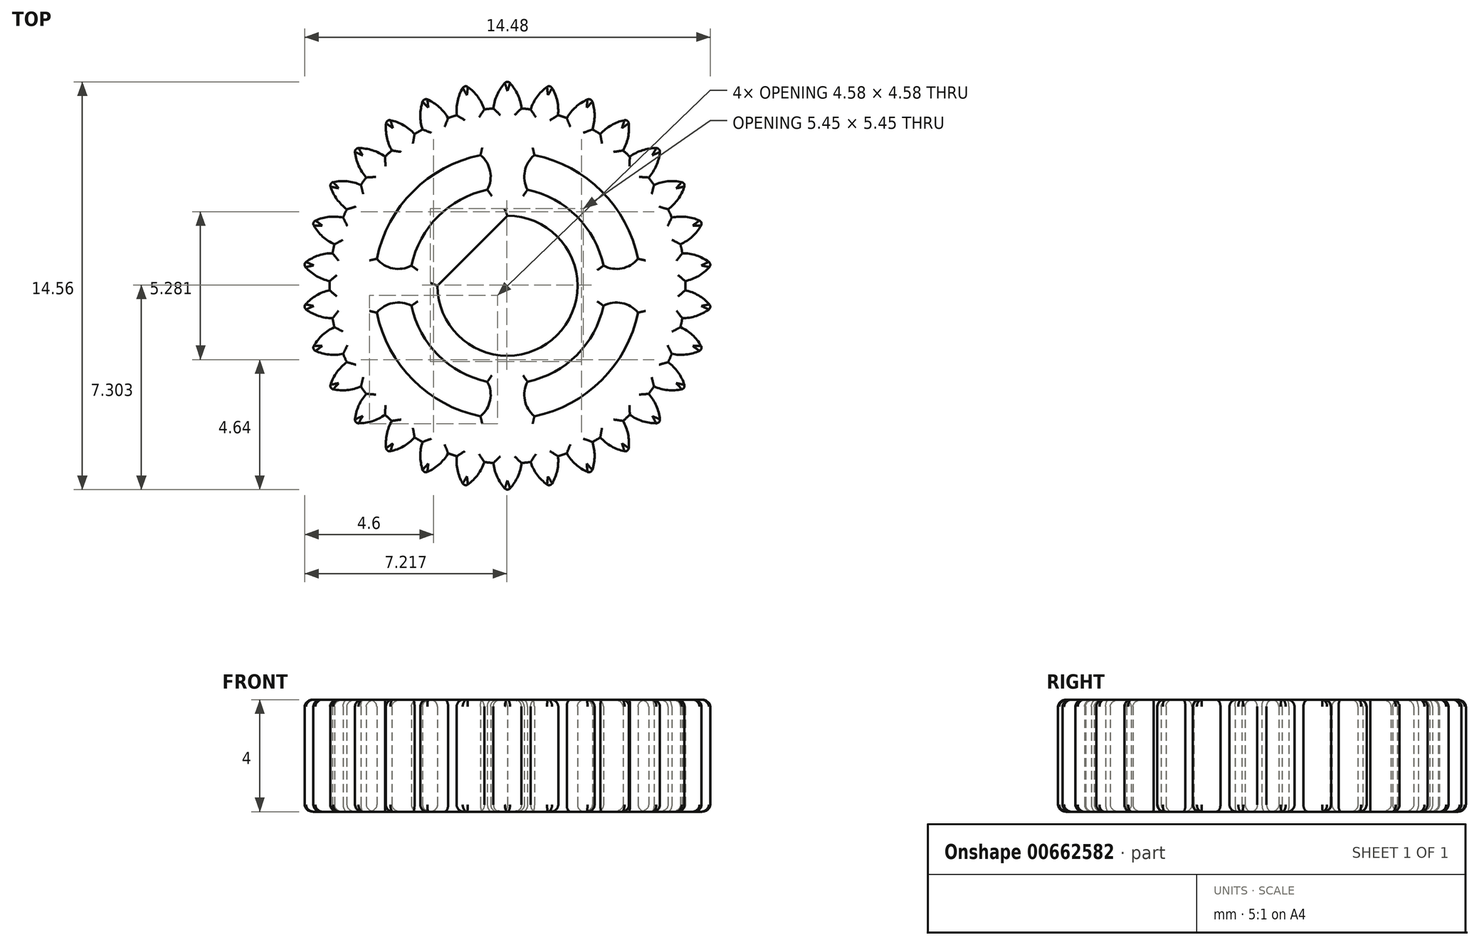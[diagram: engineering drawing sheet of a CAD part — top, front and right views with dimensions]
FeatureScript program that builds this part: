
annotation { "Feature Type Name" : "Feature", "Feature Type Description" : "" }
export const myFeature = defineFeature(function(context is Context, id is Id, definition is map)
    precondition{}
    {
        {
            var Q0;
            Q0=qCreatedBy(makeId("Top.planeOp"),FACE);
            var sketch = newSketch(context, id + "F0", { "sketchPlane" : qUnion([Q0])});
            skCircle(sketch, "E0", {"center": v(0, 0) * mm, "radius": 6.35 * mm});
            skCircle(sketch, "E1", {"center": v(0, 0) * mm, "radius": 4.76 * mm});
            skCircle(sketch, "E2", {"center": v(0, 0) * mm, "radius": 2.5 * mm});
            skCircle(sketch, "E3", {"center": v(0, 0) * mm, "radius": 3.5 * mm});
            skArc(sketch, "E4", {"start": v(-0.72, 3.43) * mm, "mid": v(-0.62, 4.09) * mm, "end": v(-0.96, 4.66) * mm});
            skLineSegment(sketch, "E5", {"start": v(0, 4.76) * mm, "end": v(0, 3.5) * mm});
            skArc(sketch, "E6.MirrorCS", {"start": v(0.72, 3.43) * mm, "mid": v(0.62, 4.09) * mm, "end": v(0.96, 4.66) * mm});
            skArc(sketch, "E7.1.0", {"start": v(-3.43, -0.72) * mm, "mid": v(-4.09, -0.62) * mm, "end": v(-4.66, -0.96) * mm});
            skArc(sketch, "E7.1.1", {"start": v(-3.43, 0.72) * mm, "mid": v(-4.09, 0.62) * mm, "end": v(-4.66, 0.96) * mm});
            skArc(sketch, "E7.2.0", {"start": v(0.72, -3.43) * mm, "mid": v(0.62, -4.09) * mm, "end": v(0.96, -4.66) * mm});
            skArc(sketch, "E7.2.1", {"start": v(-0.72, -3.43) * mm, "mid": v(-0.62, -4.09) * mm, "end": v(-0.96, -4.66) * mm});
            skArc(sketch, "E7.3.0", {"start": v(3.43, 0.72) * mm, "mid": v(4.09, 0.62) * mm, "end": v(4.66, 0.96) * mm});
            skArc(sketch, "E7.3.1", {"start": v(3.43, -0.72) * mm, "mid": v(4.09, -0.62) * mm, "end": v(4.66, -0.96) * mm});
            skLineSegment(sketch, "E8", {"start": v(0, 2.5) * mm, "end": v(-2.5, 0) * mm});
            skLineSegment(sketch, "E9", {"start": v(0, 7.33) * mm, "end": v(-0.5, 6.33) * mm});
            skLineSegment(sketch, "E10", {"start": v(0, 7.33) * mm, "end": v(0.5, 6.33) * mm});
            skArc(sketch, "E11", {"start": v(0, 7.33) * mm, "mid": v(-0.34, 6.88) * mm, "end": v(-0.5, 6.33) * mm});
            skLineSegment(sketch, "E12", {"start": v(0, 7.33) * mm, "end": v(0, 6.35) * mm});
            skArc(sketch, "E13.MirrorCS", {"start": v(0, 7.33) * mm, "mid": v(0.34, 6.88) * mm, "end": v(0.5, 6.33) * mm});
            skLineSegment(sketch, "E14.1.0", {"start": v(-1.52, 7.17) * mm, "end": v(-1.8, 6.09) * mm});
            skLineSegment(sketch, "E14.1.1", {"start": v(-1.52, 7.17) * mm, "end": v(-0.83, 6.3) * mm});
            skArc(sketch, "E14.1.2", {"start": v(-1.52, 7.17) * mm, "mid": v(-1.76, 6.65) * mm, "end": v(-1.8, 6.09) * mm});
            skArc(sketch, "E14.1.3", {"start": v(-1.52, 7.17) * mm, "mid": v(-1.1, 6.8) * mm, "end": v(-0.83, 6.3) * mm});
            skLineSegment(sketch, "E14.2.0", {"start": v(-2.98, 6.7) * mm, "end": v(-3.03, 5.58) * mm});
            skLineSegment(sketch, "E14.2.1", {"start": v(-2.98, 6.7) * mm, "end": v(-2.12, 5.99) * mm});
            skArc(sketch, "E14.2.2", {"start": v(-2.98, 6.7) * mm, "mid": v(-3.1, 6.14) * mm, "end": v(-3.03, 5.58) * mm});
            skArc(sketch, "E14.2.3", {"start": v(-2.98, 6.7) * mm, "mid": v(-2.49, 6.42) * mm, "end": v(-2.12, 5.99) * mm});
            skLineSegment(sketch, "E14.3.0", {"start": v(-4.3, 5.93) * mm, "end": v(-4.13, 4.83) * mm});
            skLineSegment(sketch, "E14.3.1", {"start": v(-4.3, 5.93) * mm, "end": v(-3.32, 5.42) * mm});
            skArc(sketch, "E14.3.2", {"start": v(-4.3, 5.93) * mm, "mid": v(-4.32, 5.36) * mm, "end": v(-4.13, 4.83) * mm});
            skArc(sketch, "E14.3.3", {"start": v(-4.3, 5.93) * mm, "mid": v(-3.77, 5.76) * mm, "end": v(-3.32, 5.42) * mm});
            skLineSegment(sketch, "E14.4.0", {"start": v(-5.45, 4.9) * mm, "end": v(-5.04, 3.86) * mm});
            skLineSegment(sketch, "E14.4.1", {"start": v(-5.45, 4.9) * mm, "end": v(-4.37, 4.6) * mm});
            skArc(sketch, "E14.4.2", {"start": v(-5.45, 4.9) * mm, "mid": v(-5.34, 4.35) * mm, "end": v(-5.04, 3.86) * mm});
            skArc(sketch, "E14.4.3", {"start": v(-5.45, 4.9) * mm, "mid": v(-4.88, 4.85) * mm, "end": v(-4.37, 4.6) * mm});
            skLineSegment(sketch, "E14.5.0", {"start": v(-6.35, 3.67) * mm, "end": v(-5.73, 2.73) * mm});
            skLineSegment(sketch, "E14.5.1", {"start": v(-6.35, 3.67) * mm, "end": v(-5.23, 3.6) * mm});
            skArc(sketch, "E14.5.2", {"start": v(-6.35, 3.67) * mm, "mid": v(-6.13, 3.14) * mm, "end": v(-5.73, 2.73) * mm});
            skArc(sketch, "E14.5.3", {"start": v(-6.35, 3.67) * mm, "mid": v(-5.78, 3.73) * mm, "end": v(-5.23, 3.6) * mm});
            skLineSegment(sketch, "E14.6.0", {"start": v(-6.97, 2.27) * mm, "end": v(-6.17, 1.48) * mm});
            skLineSegment(sketch, "E14.6.1", {"start": v(-6.97, 2.27) * mm, "end": v(-5.87, 2.43) * mm});
            skArc(sketch, "E14.6.2", {"start": v(-6.97, 2.27) * mm, "mid": v(-6.64, 1.8) * mm, "end": v(-6.17, 1.48) * mm});
            skArc(sketch, "E14.6.3", {"start": v(-6.97, 2.27) * mm, "mid": v(-6.43, 2.45) * mm, "end": v(-5.87, 2.43) * mm});
            skLineSegment(sketch, "E14.7.0", {"start": v(-7.3, 0.77) * mm, "end": v(-6.35, 0.16) * mm});
            skLineSegment(sketch, "E14.7.1", {"start": v(-7.3, 0.77) * mm, "end": v(-6.24, 1.16) * mm});
            skArc(sketch, "E14.7.2", {"start": v(-7.3, 0.77) * mm, "mid": v(-6.87, 0.38) * mm, "end": v(-6.35, 0.16) * mm});
            skArc(sketch, "E14.7.3", {"start": v(-7.3, 0.77) * mm, "mid": v(-6.8, 1.06) * mm, "end": v(-6.24, 1.16) * mm});
            skLineSegment(sketch, "E14.8.0", {"start": v(-7.3, -0.77) * mm, "end": v(-6.24, -1.16) * mm});
            skLineSegment(sketch, "E14.8.1", {"start": v(-7.3, -0.77) * mm, "end": v(-6.35, -0.16) * mm});
            skArc(sketch, "E14.8.2", {"start": v(-7.3, -0.77) * mm, "mid": v(-6.8, -1.06) * mm, "end": v(-6.24, -1.16) * mm});
            skArc(sketch, "E14.8.3", {"start": v(-7.3, -0.77) * mm, "mid": v(-6.87, -0.38) * mm, "end": v(-6.35, -0.16) * mm});
            skLineSegment(sketch, "E14.9.0", {"start": v(-6.97, -2.27) * mm, "end": v(-5.87, -2.43) * mm});
            skLineSegment(sketch, "E14.9.1", {"start": v(-6.97, -2.27) * mm, "end": v(-6.17, -1.48) * mm});
            skArc(sketch, "E14.9.2", {"start": v(-6.97, -2.27) * mm, "mid": v(-6.43, -2.45) * mm, "end": v(-5.87, -2.43) * mm});
            skArc(sketch, "E14.9.3", {"start": v(-6.97, -2.27) * mm, "mid": v(-6.64, -1.8) * mm, "end": v(-6.17, -1.48) * mm});
            skLineSegment(sketch, "E14.10.0", {"start": v(-6.35, -3.67) * mm, "end": v(-5.23, -3.6) * mm});
            skLineSegment(sketch, "E14.10.1", {"start": v(-6.35, -3.67) * mm, "end": v(-5.73, -2.73) * mm});
            skArc(sketch, "E14.10.2", {"start": v(-6.35, -3.67) * mm, "mid": v(-5.78, -3.73) * mm, "end": v(-5.23, -3.6) * mm});
            skArc(sketch, "E14.10.3", {"start": v(-6.35, -3.67) * mm, "mid": v(-6.13, -3.14) * mm, "end": v(-5.73, -2.73) * mm});
            skLineSegment(sketch, "E14.11.0", {"start": v(-5.45, -4.9) * mm, "end": v(-4.37, -4.6) * mm});
            skLineSegment(sketch, "E14.11.1", {"start": v(-5.45, -4.9) * mm, "end": v(-5.04, -3.86) * mm});
            skArc(sketch, "E14.11.2", {"start": v(-5.45, -4.9) * mm, "mid": v(-4.88, -4.85) * mm, "end": v(-4.37, -4.6) * mm});
            skArc(sketch, "E14.11.3", {"start": v(-5.45, -4.9) * mm, "mid": v(-5.34, -4.35) * mm, "end": v(-5.04, -3.86) * mm});
            skLineSegment(sketch, "E14.12.0", {"start": v(-4.3, -5.93) * mm, "end": v(-3.32, -5.42) * mm});
            skLineSegment(sketch, "E14.12.1", {"start": v(-4.3, -5.93) * mm, "end": v(-4.13, -4.83) * mm});
            skArc(sketch, "E14.12.2", {"start": v(-4.3, -5.93) * mm, "mid": v(-3.77, -5.76) * mm, "end": v(-3.32, -5.42) * mm});
            skArc(sketch, "E14.12.3", {"start": v(-4.3, -5.93) * mm, "mid": v(-4.32, -5.36) * mm, "end": v(-4.13, -4.83) * mm});
            skLineSegment(sketch, "E14.13.0", {"start": v(-2.98, -6.7) * mm, "end": v(-2.12, -5.99) * mm});
            skLineSegment(sketch, "E14.13.1", {"start": v(-2.98, -6.7) * mm, "end": v(-3.03, -5.58) * mm});
            skArc(sketch, "E14.13.2", {"start": v(-2.98, -6.7) * mm, "mid": v(-2.49, -6.42) * mm, "end": v(-2.12, -5.99) * mm});
            skArc(sketch, "E14.13.3", {"start": v(-2.98, -6.7) * mm, "mid": v(-3.1, -6.14) * mm, "end": v(-3.03, -5.58) * mm});
            skLineSegment(sketch, "E14.14.0", {"start": v(-1.52, -7.17) * mm, "end": v(-0.83, -6.3) * mm});
            skLineSegment(sketch, "E14.14.1", {"start": v(-1.52, -7.17) * mm, "end": v(-1.8, -6.09) * mm});
            skArc(sketch, "E14.14.2", {"start": v(-1.52, -7.17) * mm, "mid": v(-1.1, -6.8) * mm, "end": v(-0.83, -6.3) * mm});
            skArc(sketch, "E14.14.3", {"start": v(-1.52, -7.17) * mm, "mid": v(-1.76, -6.65) * mm, "end": v(-1.8, -6.09) * mm});
            skLineSegment(sketch, "E14.15.0", {"start": v(0, -7.33) * mm, "end": v(0.5, -6.33) * mm});
            skLineSegment(sketch, "E14.15.1", {"start": v(0, -7.33) * mm, "end": v(-0.5, -6.33) * mm});
            skArc(sketch, "E14.15.2", {"start": v(0, -7.33) * mm, "mid": v(0.34, -6.88) * mm, "end": v(0.5, -6.33) * mm});
            skArc(sketch, "E14.15.3", {"start": v(0, -7.33) * mm, "mid": v(-0.34, -6.88) * mm, "end": v(-0.5, -6.33) * mm});
            skLineSegment(sketch, "E14.16.0", {"start": v(1.52, -7.17) * mm, "end": v(1.8, -6.09) * mm});
            skLineSegment(sketch, "E14.16.1", {"start": v(1.52, -7.17) * mm, "end": v(0.83, -6.3) * mm});
            skArc(sketch, "E14.16.2", {"start": v(1.52, -7.17) * mm, "mid": v(1.76, -6.65) * mm, "end": v(1.8, -6.09) * mm});
            skArc(sketch, "E14.16.3", {"start": v(1.52, -7.17) * mm, "mid": v(1.1, -6.8) * mm, "end": v(0.83, -6.3) * mm});
            skLineSegment(sketch, "E14.17.0", {"start": v(2.98, -6.7) * mm, "end": v(3.03, -5.58) * mm});
            skLineSegment(sketch, "E14.17.1", {"start": v(2.98, -6.7) * mm, "end": v(2.12, -5.99) * mm});
            skArc(sketch, "E14.17.2", {"start": v(2.98, -6.7) * mm, "mid": v(3.1, -6.14) * mm, "end": v(3.03, -5.58) * mm});
            skArc(sketch, "E14.17.3", {"start": v(2.98, -6.7) * mm, "mid": v(2.49, -6.42) * mm, "end": v(2.12, -5.99) * mm});
            skLineSegment(sketch, "E14.18.0", {"start": v(4.3, -5.93) * mm, "end": v(4.13, -4.83) * mm});
            skLineSegment(sketch, "E14.18.1", {"start": v(4.3, -5.93) * mm, "end": v(3.32, -5.42) * mm});
            skArc(sketch, "E14.18.2", {"start": v(4.3, -5.93) * mm, "mid": v(4.32, -5.36) * mm, "end": v(4.13, -4.83) * mm});
            skArc(sketch, "E14.18.3", {"start": v(4.3, -5.93) * mm, "mid": v(3.77, -5.76) * mm, "end": v(3.32, -5.42) * mm});
            skLineSegment(sketch, "E14.19.0", {"start": v(5.45, -4.9) * mm, "end": v(5.04, -3.86) * mm});
            skLineSegment(sketch, "E14.19.1", {"start": v(5.45, -4.9) * mm, "end": v(4.37, -4.6) * mm});
            skArc(sketch, "E14.19.2", {"start": v(5.45, -4.9) * mm, "mid": v(5.34, -4.35) * mm, "end": v(5.04, -3.86) * mm});
            skArc(sketch, "E14.19.3", {"start": v(5.45, -4.9) * mm, "mid": v(4.88, -4.85) * mm, "end": v(4.37, -4.6) * mm});
            skLineSegment(sketch, "E14.20.0", {"start": v(6.35, -3.67) * mm, "end": v(5.73, -2.73) * mm});
            skLineSegment(sketch, "E14.20.1", {"start": v(6.35, -3.67) * mm, "end": v(5.23, -3.6) * mm});
            skArc(sketch, "E14.20.2", {"start": v(6.35, -3.67) * mm, "mid": v(6.13, -3.14) * mm, "end": v(5.73, -2.73) * mm});
            skArc(sketch, "E14.20.3", {"start": v(6.35, -3.67) * mm, "mid": v(5.78, -3.73) * mm, "end": v(5.23, -3.6) * mm});
            skLineSegment(sketch, "E14.21.0", {"start": v(6.97, -2.27) * mm, "end": v(6.17, -1.48) * mm});
            skLineSegment(sketch, "E14.21.1", {"start": v(6.97, -2.27) * mm, "end": v(5.87, -2.43) * mm});
            skArc(sketch, "E14.21.2", {"start": v(6.97, -2.27) * mm, "mid": v(6.64, -1.8) * mm, "end": v(6.17, -1.48) * mm});
            skArc(sketch, "E14.21.3", {"start": v(6.97, -2.27) * mm, "mid": v(6.43, -2.45) * mm, "end": v(5.87, -2.43) * mm});
            skLineSegment(sketch, "E14.22.0", {"start": v(7.3, -0.77) * mm, "end": v(6.35, -0.16) * mm});
            skLineSegment(sketch, "E14.22.1", {"start": v(7.3, -0.77) * mm, "end": v(6.24, -1.16) * mm});
            skArc(sketch, "E14.22.2", {"start": v(7.3, -0.77) * mm, "mid": v(6.87, -0.38) * mm, "end": v(6.35, -0.16) * mm});
            skArc(sketch, "E14.22.3", {"start": v(7.3, -0.77) * mm, "mid": v(6.8, -1.06) * mm, "end": v(6.24, -1.16) * mm});
            skLineSegment(sketch, "E14.23.0", {"start": v(7.3, 0.77) * mm, "end": v(6.24, 1.16) * mm});
            skLineSegment(sketch, "E14.23.1", {"start": v(7.3, 0.77) * mm, "end": v(6.35, 0.16) * mm});
            skArc(sketch, "E14.23.2", {"start": v(7.3, 0.77) * mm, "mid": v(6.8, 1.06) * mm, "end": v(6.24, 1.16) * mm});
            skArc(sketch, "E14.23.3", {"start": v(7.3, 0.77) * mm, "mid": v(6.87, 0.38) * mm, "end": v(6.35, 0.16) * mm});
            skLineSegment(sketch, "E14.24.0", {"start": v(6.97, 2.27) * mm, "end": v(5.87, 2.43) * mm});
            skLineSegment(sketch, "E14.24.1", {"start": v(6.97, 2.27) * mm, "end": v(6.17, 1.48) * mm});
            skArc(sketch, "E14.24.2", {"start": v(6.97, 2.27) * mm, "mid": v(6.43, 2.45) * mm, "end": v(5.87, 2.43) * mm});
            skArc(sketch, "E14.24.3", {"start": v(6.97, 2.27) * mm, "mid": v(6.64, 1.8) * mm, "end": v(6.17, 1.48) * mm});
            skLineSegment(sketch, "E14.25.0", {"start": v(6.35, 3.67) * mm, "end": v(5.23, 3.6) * mm});
            skLineSegment(sketch, "E14.25.1", {"start": v(6.35, 3.67) * mm, "end": v(5.73, 2.73) * mm});
            skArc(sketch, "E14.25.2", {"start": v(6.35, 3.67) * mm, "mid": v(5.78, 3.73) * mm, "end": v(5.23, 3.6) * mm});
            skArc(sketch, "E14.25.3", {"start": v(6.35, 3.67) * mm, "mid": v(6.13, 3.14) * mm, "end": v(5.73, 2.73) * mm});
            skLineSegment(sketch, "E14.26.0", {"start": v(5.45, 4.9) * mm, "end": v(4.37, 4.6) * mm});
            skLineSegment(sketch, "E14.26.1", {"start": v(5.45, 4.9) * mm, "end": v(5.04, 3.86) * mm});
            skArc(sketch, "E14.26.2", {"start": v(5.45, 4.9) * mm, "mid": v(4.88, 4.85) * mm, "end": v(4.37, 4.6) * mm});
            skArc(sketch, "E14.26.3", {"start": v(5.45, 4.9) * mm, "mid": v(5.34, 4.35) * mm, "end": v(5.04, 3.86) * mm});
            skLineSegment(sketch, "E14.27.0", {"start": v(4.3, 5.93) * mm, "end": v(3.32, 5.42) * mm});
            skLineSegment(sketch, "E14.27.1", {"start": v(4.3, 5.93) * mm, "end": v(4.13, 4.83) * mm});
            skArc(sketch, "E14.27.2", {"start": v(4.3, 5.93) * mm, "mid": v(3.77, 5.76) * mm, "end": v(3.32, 5.42) * mm});
            skArc(sketch, "E14.27.3", {"start": v(4.3, 5.93) * mm, "mid": v(4.32, 5.36) * mm, "end": v(4.13, 4.83) * mm});
            skLineSegment(sketch, "E14.28.0", {"start": v(2.98, 6.7) * mm, "end": v(2.12, 5.99) * mm});
            skLineSegment(sketch, "E14.28.1", {"start": v(2.98, 6.7) * mm, "end": v(3.03, 5.58) * mm});
            skArc(sketch, "E14.28.2", {"start": v(2.98, 6.7) * mm, "mid": v(2.49, 6.42) * mm, "end": v(2.12, 5.99) * mm});
            skArc(sketch, "E14.28.3", {"start": v(2.98, 6.7) * mm, "mid": v(3.1, 6.14) * mm, "end": v(3.03, 5.58) * mm});
            skLineSegment(sketch, "E14.29.0", {"start": v(1.52, 7.17) * mm, "end": v(0.83, 6.3) * mm});
            skLineSegment(sketch, "E14.29.1", {"start": v(1.52, 7.17) * mm, "end": v(1.8, 6.09) * mm});
            skArc(sketch, "E14.29.2", {"start": v(1.52, 7.17) * mm, "mid": v(1.1, 6.8) * mm, "end": v(0.83, 6.3) * mm});
            skArc(sketch, "E14.29.3", {"start": v(1.52, 7.17) * mm, "mid": v(1.76, 6.65) * mm, "end": v(1.8, 6.09) * mm});
            skSolve(sketch);
        }
        {
            var Q0;
            Q0 = qSketchRegion(id + "F0", true);
            var Q1;
            {var subQ0=sQuery(id+"F0.wireOp",EDGE,"E4");Q1=makeQuery(id+"F0.imprint","IMPRINT",FACE,{"disambiguationData":[TD([[makeQuery(id+"F0.imprint","IMPRINT",EDGE,{"derivedFrom":subQ0}),-1.0]])]});}
            var Q2;
            {var subQ0=sQuery(id+"F0.wireOp",EDGE,"E5");Q2=makeQuery(id+"F0.imprint","IMPRINT",FACE,{"disambiguationData":[TD([[makeQuery(id+"F0.imprint","IMPRINT",EDGE,{"derivedFrom":subQ0}),1.0]])]});}
            var Q3;
            {var subQ0=sQuery(id+"F0.wireOp",EDGE,"E7.1.0");Q3=makeQuery(id+"F0.imprint","IMPRINT",FACE,{"disambiguationData":[TD([[makeQuery(id+"F0.imprint","IMPRINT",EDGE,{"derivedFrom":subQ0}),-1.0]])]});}
            var Q4;
            {var subQ0=sQuery(id+"F0.wireOp",EDGE,"E7.3.0");Q4=makeQuery(id+"F0.imprint","IMPRINT",FACE,{"disambiguationData":[TD([[makeQuery(id+"F0.imprint","IMPRINT",EDGE,{"derivedFrom":subQ0}),-1.0]])]});}
            var Q5;
            {var subQ0=sQuery(id+"F0.wireOp",EDGE,"E7.2.0");Q5=makeQuery(id+"F0.imprint","IMPRINT",FACE,{"disambiguationData":[TD([[makeQuery(id+"F0.imprint","IMPRINT",EDGE,{"derivedFrom":subQ0}),-1.0]])]});}
            var Q6;
            {var subQ8=sQuery(id+"F0.wireOp",EDGE,"E8");var subQ9=sQuery(id+"F0.wireOp",EDGE,"E2");var subQ10=makeQuery(id+"F0.imprint","INTERSECT",VERTEX,{"disambiguationData":[OD(0.0)],"derivedFrom":[subQ9,subQ8]});Q6=makeQuery(id+"F0.imprint","IMPRINT",FACE,{"disambiguationData":[TD([[makeQuery(id+"F0.imprint","IMPRINT",EDGE,{"disambiguationData":[TD([[subQ10,-1.0]])],"derivedFrom":subQ9}),-1.0]])]});}
            var Q7;
            {var subQ0=sQuery(id+"F0.wireOp",EDGE,"E8");Q7=makeQuery(id+"F0.imprint","IMPRINT",FACE,{"disambiguationData":[TD([[makeQuery(id+"F0.imprint","IMPRINT",EDGE,{"derivedFrom":subQ0}),-1.0]])]});}
            extrude(context, id + "F1", {"entities" : qUnion([Q0, Q1, Q2, Q3, Q4, Q5, Q6, Q7]), "depth" : 4 * mm, "offsetDistance" : 25.4 * mm});
        }
        {
            var Q0;
            Q0=makeQuery(id+"F1.opExtrude","CAP_FACE",FACE,{"disambiguationData":[OSD([sQuery(id+"F0.wireOp",EDGE,"E0"),sQuery(id+"F0.wireOp",EDGE,"E1"),sQuery(id+"F0.wireOp",EDGE,"E2"),sQuery(id+"F0.wireOp",EDGE,"E3"),sQuery(id+"F0.wireOp",EDGE,"E4"),sQuery(id+"F0.wireOp",EDGE,"E6.MirrorCS"),sQuery(id+"F0.wireOp",EDGE,"E7.1.0"),sQuery(id+"F0.wireOp",EDGE,"E7.1.1"),sQuery(id+"F0.wireOp",EDGE,"E7.2.0"),sQuery(id+"F0.wireOp",EDGE,"E7.2.1"),sQuery(id+"F0.wireOp",EDGE,"E7.3.0"),sQuery(id+"F0.wireOp",EDGE,"E7.3.1"),sQuery(id+"F0.wireOp",EDGE,"E8")])],"isStart":false});
            var Q1;
            Q1=makeQuery(id+"F1.opExtrude","CAP_FACE",FACE,{"disambiguationData":[OSD([sQuery(id+"F0.wireOp",EDGE,"E0"),sQuery(id+"F0.wireOp",EDGE,"E1"),sQuery(id+"F0.wireOp",EDGE,"E2"),sQuery(id+"F0.wireOp",EDGE,"E3"),sQuery(id+"F0.wireOp",EDGE,"E4"),sQuery(id+"F0.wireOp",EDGE,"E6.MirrorCS"),sQuery(id+"F0.wireOp",EDGE,"E7.1.0"),sQuery(id+"F0.wireOp",EDGE,"E7.1.1"),sQuery(id+"F0.wireOp",EDGE,"E7.2.0"),sQuery(id+"F0.wireOp",EDGE,"E7.2.1"),sQuery(id+"F0.wireOp",EDGE,"E7.3.0"),sQuery(id+"F0.wireOp",EDGE,"E7.3.1"),sQuery(id+"F0.wireOp",EDGE,"E8")])],"isStart":true});
            fillet(context, id + "F2", {"entities" : qUnion([Q0, Q1]), "radius" : 0.25 * mm, "tangentPropagation" : true, "allowEdgeOverflow" : false});
        }
        {
            var Q0;
            Q0=makeQuery(id+"F1.opExtrude","SWEPT_EDGE",EDGE,{"disambiguationData":[OSD([sQuery(id+"F0.wireOp",EDGE,"E9"),sQuery(id+"F0.wireOp",EDGE,"E10"),sQuery(id+"F0.wireOp",EDGE,"E11"),sQuery(id+"F0.wireOp",EDGE,"E12"),sQuery(id+"F0.wireOp",EDGE,"E13.MirrorCS")])]});
            var Q1;
            Q1=makeQuery(id+"F1.opExtrude","SWEPT_EDGE",EDGE,{"disambiguationData":[OSD([sQuery(id+"F0.wireOp",EDGE,"E14.1.0"),sQuery(id+"F0.wireOp",EDGE,"E14.1.1"),sQuery(id+"F0.wireOp",EDGE,"E14.1.2"),sQuery(id+"F0.wireOp",EDGE,"E14.1.3")])]});
            var Q2;
            Q2=makeQuery(id+"F1.opExtrude","SWEPT_EDGE",EDGE,{"disambiguationData":[OSD([sQuery(id+"F0.wireOp",EDGE,"E14.29.0"),sQuery(id+"F0.wireOp",EDGE,"E14.29.1"),sQuery(id+"F0.wireOp",EDGE,"E14.29.2"),sQuery(id+"F0.wireOp",EDGE,"E14.29.3")])]});
            var Q3;
            Q3=makeQuery(id+"F1.opExtrude","SWEPT_EDGE",EDGE,{"disambiguationData":[OSD([sQuery(id+"F0.wireOp",EDGE,"E14.28.0"),sQuery(id+"F0.wireOp",EDGE,"E14.28.1"),sQuery(id+"F0.wireOp",EDGE,"E14.28.2"),sQuery(id+"F0.wireOp",EDGE,"E14.28.3")])]});
            var Q4;
            Q4=makeQuery(id+"F1.opExtrude","SWEPT_EDGE",EDGE,{"disambiguationData":[OSD([sQuery(id+"F0.wireOp",EDGE,"E14.2.0"),sQuery(id+"F0.wireOp",EDGE,"E14.2.1"),sQuery(id+"F0.wireOp",EDGE,"E14.2.2"),sQuery(id+"F0.wireOp",EDGE,"E14.2.3")])]});
            var Q5;
            Q5=makeQuery(id+"F1.opExtrude","SWEPT_EDGE",EDGE,{"disambiguationData":[OSD([sQuery(id+"F0.wireOp",EDGE,"E14.3.0"),sQuery(id+"F0.wireOp",EDGE,"E14.3.1"),sQuery(id+"F0.wireOp",EDGE,"E14.3.2"),sQuery(id+"F0.wireOp",EDGE,"E14.3.3")])]});
            var Q6;
            Q6=makeQuery(id+"F1.opExtrude","SWEPT_EDGE",EDGE,{"disambiguationData":[OSD([sQuery(id+"F0.wireOp",EDGE,"E14.4.0"),sQuery(id+"F0.wireOp",EDGE,"E14.4.1"),sQuery(id+"F0.wireOp",EDGE,"E14.4.2"),sQuery(id+"F0.wireOp",EDGE,"E14.4.3")])]});
            var Q7;
            Q7=makeQuery(id+"F1.opExtrude","SWEPT_EDGE",EDGE,{"disambiguationData":[OSD([sQuery(id+"F0.wireOp",EDGE,"E14.5.0"),sQuery(id+"F0.wireOp",EDGE,"E14.5.1"),sQuery(id+"F0.wireOp",EDGE,"E14.5.2"),sQuery(id+"F0.wireOp",EDGE,"E14.5.3")])]});
            var Q8;
            Q8=makeQuery(id+"F1.opExtrude","SWEPT_EDGE",EDGE,{"disambiguationData":[OSD([sQuery(id+"F0.wireOp",EDGE,"E14.6.0"),sQuery(id+"F0.wireOp",EDGE,"E14.6.1"),sQuery(id+"F0.wireOp",EDGE,"E14.6.2"),sQuery(id+"F0.wireOp",EDGE,"E14.6.3")])]});
            var Q9;
            Q9=makeQuery(id+"F1.opExtrude","SWEPT_EDGE",EDGE,{"disambiguationData":[OSD([sQuery(id+"F0.wireOp",EDGE,"E14.27.0"),sQuery(id+"F0.wireOp",EDGE,"E14.27.1"),sQuery(id+"F0.wireOp",EDGE,"E14.27.2"),sQuery(id+"F0.wireOp",EDGE,"E14.27.3")])]});
            var Q10;
            Q10=makeQuery(id+"F1.opExtrude","SWEPT_EDGE",EDGE,{"disambiguationData":[OSD([sQuery(id+"F0.wireOp",EDGE,"E14.26.0"),sQuery(id+"F0.wireOp",EDGE,"E14.26.1"),sQuery(id+"F0.wireOp",EDGE,"E14.26.2"),sQuery(id+"F0.wireOp",EDGE,"E14.26.3")])]});
            var Q11;
            Q11=makeQuery(id+"F1.opExtrude","SWEPT_EDGE",EDGE,{"disambiguationData":[OSD([sQuery(id+"F0.wireOp",EDGE,"E14.25.0"),sQuery(id+"F0.wireOp",EDGE,"E14.25.1"),sQuery(id+"F0.wireOp",EDGE,"E14.25.2"),sQuery(id+"F0.wireOp",EDGE,"E14.25.3")])]});
            var Q12;
            Q12=makeQuery(id+"F1.opExtrude","SWEPT_EDGE",EDGE,{"disambiguationData":[OSD([sQuery(id+"F0.wireOp",EDGE,"E14.24.0"),sQuery(id+"F0.wireOp",EDGE,"E14.24.1"),sQuery(id+"F0.wireOp",EDGE,"E14.24.2"),sQuery(id+"F0.wireOp",EDGE,"E14.24.3")])]});
            var Q13;
            Q13=makeQuery(id+"F1.opExtrude","SWEPT_EDGE",EDGE,{"disambiguationData":[OSD([sQuery(id+"F0.wireOp",EDGE,"E14.23.0"),sQuery(id+"F0.wireOp",EDGE,"E14.23.1"),sQuery(id+"F0.wireOp",EDGE,"E14.23.2"),sQuery(id+"F0.wireOp",EDGE,"E14.23.3")])]});
            var Q14;
            Q14=makeQuery(id+"F1.opExtrude","SWEPT_EDGE",EDGE,{"disambiguationData":[OSD([sQuery(id+"F0.wireOp",EDGE,"E14.22.0"),sQuery(id+"F0.wireOp",EDGE,"E14.22.1"),sQuery(id+"F0.wireOp",EDGE,"E14.22.2"),sQuery(id+"F0.wireOp",EDGE,"E14.22.3")])]});
            var Q15;
            Q15=makeQuery(id+"F1.opExtrude","SWEPT_EDGE",EDGE,{"disambiguationData":[OSD([sQuery(id+"F0.wireOp",EDGE,"E14.21.0"),sQuery(id+"F0.wireOp",EDGE,"E14.21.1"),sQuery(id+"F0.wireOp",EDGE,"E14.21.2"),sQuery(id+"F0.wireOp",EDGE,"E14.21.3")])]});
            var Q16;
            Q16=makeQuery(id+"F1.opExtrude","SWEPT_EDGE",EDGE,{"disambiguationData":[OSD([sQuery(id+"F0.wireOp",EDGE,"E14.20.0"),sQuery(id+"F0.wireOp",EDGE,"E14.20.1"),sQuery(id+"F0.wireOp",EDGE,"E14.20.2"),sQuery(id+"F0.wireOp",EDGE,"E14.20.3")])]});
            var Q17;
            Q17=makeQuery(id+"F1.opExtrude","SWEPT_EDGE",EDGE,{"disambiguationData":[OSD([sQuery(id+"F0.wireOp",EDGE,"E14.7.0"),sQuery(id+"F0.wireOp",EDGE,"E14.7.1"),sQuery(id+"F0.wireOp",EDGE,"E14.7.2"),sQuery(id+"F0.wireOp",EDGE,"E14.7.3")])]});
            var Q18;
            Q18=makeQuery(id+"F1.opExtrude","SWEPT_EDGE",EDGE,{"disambiguationData":[OSD([sQuery(id+"F0.wireOp",EDGE,"E14.8.0"),sQuery(id+"F0.wireOp",EDGE,"E14.8.1"),sQuery(id+"F0.wireOp",EDGE,"E14.8.2"),sQuery(id+"F0.wireOp",EDGE,"E14.8.3")])]});
            var Q19;
            Q19=makeQuery(id+"F1.opExtrude","SWEPT_EDGE",EDGE,{"disambiguationData":[OSD([sQuery(id+"F0.wireOp",EDGE,"E14.9.0"),sQuery(id+"F0.wireOp",EDGE,"E14.9.1"),sQuery(id+"F0.wireOp",EDGE,"E14.9.2"),sQuery(id+"F0.wireOp",EDGE,"E14.9.3")])]});
            var Q20;
            Q20=makeQuery(id+"F1.opExtrude","SWEPT_EDGE",EDGE,{"disambiguationData":[OSD([sQuery(id+"F0.wireOp",EDGE,"E14.10.0"),sQuery(id+"F0.wireOp",EDGE,"E14.10.1"),sQuery(id+"F0.wireOp",EDGE,"E14.10.2"),sQuery(id+"F0.wireOp",EDGE,"E14.10.3")])]});
            var Q21;
            Q21=makeQuery(id+"F1.opExtrude","SWEPT_EDGE",EDGE,{"disambiguationData":[OSD([sQuery(id+"F0.wireOp",EDGE,"E14.11.0"),sQuery(id+"F0.wireOp",EDGE,"E14.11.1"),sQuery(id+"F0.wireOp",EDGE,"E14.11.2"),sQuery(id+"F0.wireOp",EDGE,"E14.11.3")])]});
            var Q22;
            Q22=makeQuery(id+"F1.opExtrude","SWEPT_EDGE",EDGE,{"disambiguationData":[OSD([sQuery(id+"F0.wireOp",EDGE,"E14.13.0"),sQuery(id+"F0.wireOp",EDGE,"E14.13.1"),sQuery(id+"F0.wireOp",EDGE,"E14.13.2"),sQuery(id+"F0.wireOp",EDGE,"E14.13.3")])]});
            var Q23;
            Q23=makeQuery(id+"F1.opExtrude","SWEPT_EDGE",EDGE,{"disambiguationData":[OSD([sQuery(id+"F0.wireOp",EDGE,"E14.12.0"),sQuery(id+"F0.wireOp",EDGE,"E14.12.1"),sQuery(id+"F0.wireOp",EDGE,"E14.12.2"),sQuery(id+"F0.wireOp",EDGE,"E14.12.3")])]});
            var Q24;
            Q24=makeQuery(id+"F1.opExtrude","SWEPT_EDGE",EDGE,{"disambiguationData":[OSD([sQuery(id+"F0.wireOp",EDGE,"E14.19.0"),sQuery(id+"F0.wireOp",EDGE,"E14.19.1"),sQuery(id+"F0.wireOp",EDGE,"E14.19.2"),sQuery(id+"F0.wireOp",EDGE,"E14.19.3")])]});
            var Q25;
            Q25=makeQuery(id+"F1.opExtrude","SWEPT_EDGE",EDGE,{"disambiguationData":[OSD([sQuery(id+"F0.wireOp",EDGE,"E14.18.0"),sQuery(id+"F0.wireOp",EDGE,"E14.18.1"),sQuery(id+"F0.wireOp",EDGE,"E14.18.2"),sQuery(id+"F0.wireOp",EDGE,"E14.18.3")])]});
            var Q26;
            Q26=makeQuery(id+"F1.opExtrude","SWEPT_EDGE",EDGE,{"disambiguationData":[OSD([sQuery(id+"F0.wireOp",EDGE,"E14.17.0"),sQuery(id+"F0.wireOp",EDGE,"E14.17.1"),sQuery(id+"F0.wireOp",EDGE,"E14.17.2"),sQuery(id+"F0.wireOp",EDGE,"E14.17.3")])]});
            var Q27;
            Q27=makeQuery(id+"F1.opExtrude","SWEPT_EDGE",EDGE,{"disambiguationData":[OSD([sQuery(id+"F0.wireOp",EDGE,"E14.16.0"),sQuery(id+"F0.wireOp",EDGE,"E14.16.1"),sQuery(id+"F0.wireOp",EDGE,"E14.16.2"),sQuery(id+"F0.wireOp",EDGE,"E14.16.3")])]});
            var Q28;
            Q28=makeQuery(id+"F1.opExtrude","SWEPT_EDGE",EDGE,{"disambiguationData":[OSD([sQuery(id+"F0.wireOp",EDGE,"E14.15.0"),sQuery(id+"F0.wireOp",EDGE,"E14.15.1"),sQuery(id+"F0.wireOp",EDGE,"E14.15.2"),sQuery(id+"F0.wireOp",EDGE,"E14.15.3")])]});
            var Q29;
            Q29=makeQuery(id+"F1.opExtrude","SWEPT_EDGE",EDGE,{"disambiguationData":[OSD([sQuery(id+"F0.wireOp",EDGE,"E14.14.0"),sQuery(id+"F0.wireOp",EDGE,"E14.14.1"),sQuery(id+"F0.wireOp",EDGE,"E14.14.2"),sQuery(id+"F0.wireOp",EDGE,"E14.14.3")])]});
            fillet(context, id + "F3", {"entities" : qUnion([Q0, Q1, Q2, Q3, Q4, Q5, Q6, Q7, Q8, Q9, Q10, Q11, Q12, Q13, Q14, Q15, Q16, Q17, Q18, Q19, Q20, Q21, Q22, Q23, Q24, Q25, Q26, Q27, Q28, Q29]), "radius" : 0.12 * mm, "tangentPropagation" : true, "allowEdgeOverflow" : false});
        }
    });
